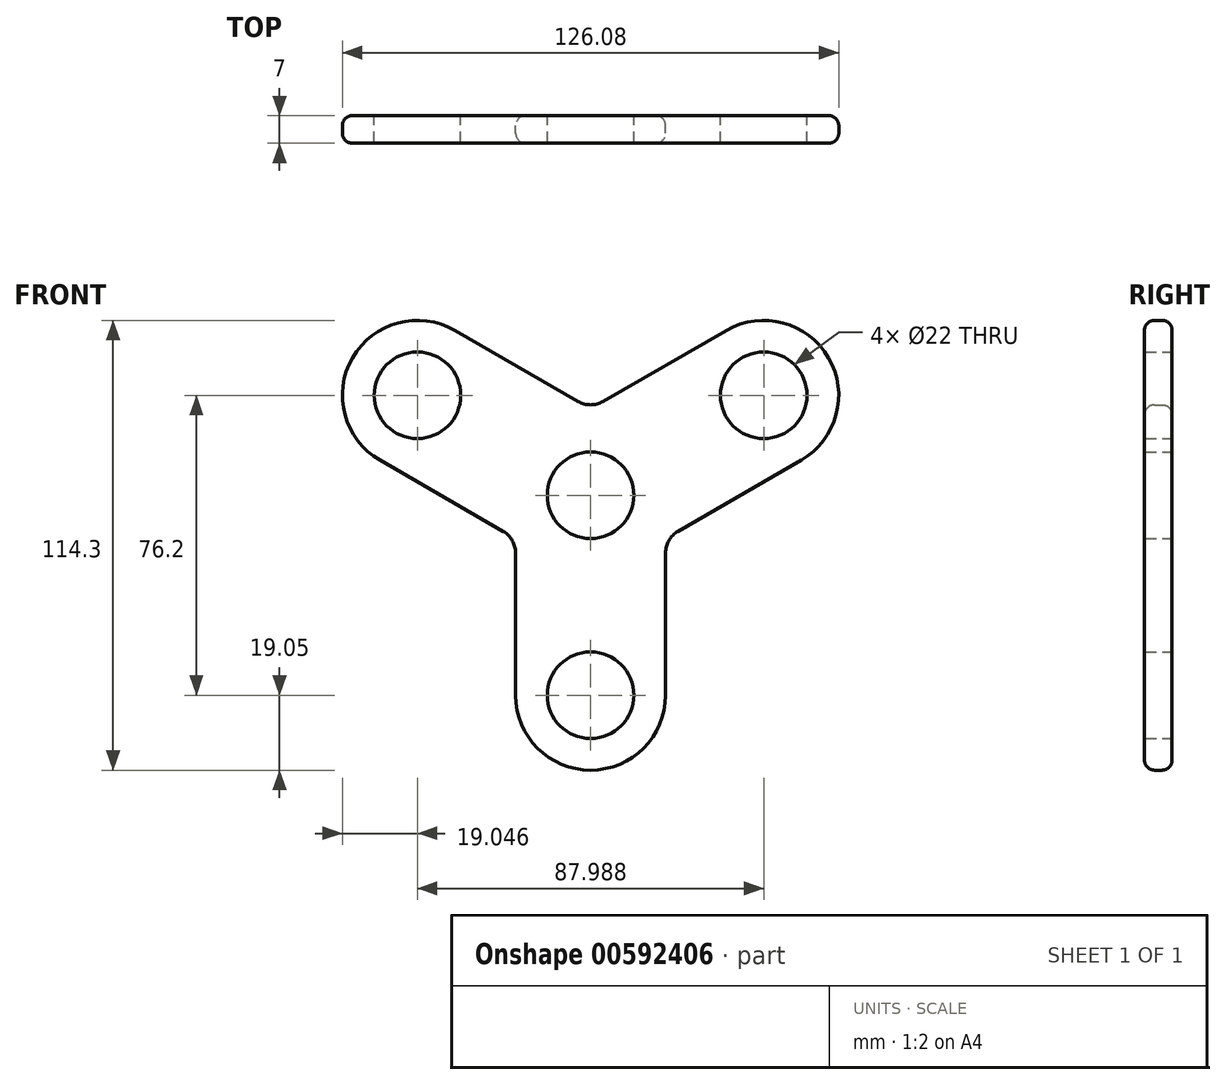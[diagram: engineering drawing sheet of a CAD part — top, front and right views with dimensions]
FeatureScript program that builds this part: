
annotation { "Feature Type Name" : "Feature", "Feature Type Description" : "" }
export const myFeature = defineFeature(function(context is Context, id is Id, definition is map)
    precondition{}
    {
        {
            var Q0;
            Q0=qCreatedBy(makeId("Front.planeOp"),FACE);
            var sketch = newSketch(context, id + "F0", { "sketchPlane" : qUnion([Q0])});
            skCircle(sketch, "E0", {"center": v(0, 6.35) * mm, "radius": 19.05 * mm});
            skCircle(sketch, "E1", {"center": v(-44, 31.75) * mm, "radius": 19.05 * mm});
            skCircle(sketch, "E2", {"center": v(44, 31.75) * mm, "radius": 19.05 * mm});
            skCircle(sketch, "E3", {"center": v(0, -44.45) * mm, "radius": 19.05 * mm});
            skLineSegment(sketch, "E4", {"start": v(-53.52, 15.25) * mm, "end": v(-22.22, -2.82) * mm});
            skLineSegment(sketch, "E5", {"start": v(22.22, -2.82) * mm, "end": v(53.52, 15.25) * mm});
            skLineSegment(sketch, "E6", {"start": v(-19.05, -8.31) * mm, "end": v(-19.05, -44.45) * mm});
            skLineSegment(sketch, "E7", {"start": v(19.05, -8.31) * mm, "end": v(19.05, -44.45) * mm});
            skLineSegment(sketch, "E8", {"start": v(0, 6.35) * mm, "end": v(-44, 31.75) * mm});
            skLineSegment(sketch, "E9", {"start": v(0, 6.35) * mm, "end": v(44, 31.75) * mm});
            skLineSegment(sketch, "E10", {"start": v(0, 6.35) * mm, "end": v(0, -44.45) * mm});
            skCircle(sketch, "E11", {"center": v(0, 6.35) * mm, "radius": 11 * mm});
            skCircle(sketch, "E12", {"center": v(44, 31.75) * mm, "radius": 11 * mm});
            skCircle(sketch, "E13", {"center": v(0, -44.45) * mm, "radius": 11 * mm});
            skCircle(sketch, "E14", {"center": v(-44, 31.75) * mm, "radius": 11 * mm});
            skArc(sketch, "E15.filletArc", {"start": v(-19.05, -8.31) * mm, "mid": v(-19.9, -5.14) * mm, "end": v(-22.22, -2.82) * mm});
            skArc(sketch, "E16.filletArc", {"start": v(22.22, -2.82) * mm, "mid": v(19.9, -5.14) * mm, "end": v(19.05, -8.31) * mm});
            skLineSegment(sketch, "E17", {"start": v(-34.47, 48.25) * mm, "end": v(-3.18, 30.18) * mm});
            skLineSegment(sketch, "E18", {"start": v(34.47, 48.25) * mm, "end": v(3.17, 30.18) * mm});
            skArc(sketch, "E19.filletArc", {"start": v(-3.18, 30.18) * mm, "mid": v(0, 29.33) * mm, "end": v(3.17, 30.18) * mm});
            skSolve(sketch);
        }
        {
            var Q0;
            Q0 = qSketchRegion(id + "F0", true);
            var Q1;
            {var subQ0=sQuery(id+"F0.wireOp",EDGE,"E8");var subQ1=sQuery(id+"F0.wireOp",EDGE,"E0");var subQ2=makeQuery(id+"F0.imprint","INTERSECT",VERTEX,{"derivedFrom":[subQ1,subQ0]});Q1=makeQuery(id+"F0.imprint","IMPRINT",FACE,{"disambiguationData":[TD([[makeQuery(id+"F0.imprint","IMPRINT",EDGE,{"disambiguationData":[TD([[subQ2,-1.0]])],"derivedFrom":subQ1}),1.0]])]});}
            var Q2;
            {var subQ0=sQuery(id+"F0.wireOp",EDGE,"E9");var subQ1=sQuery(id+"F0.wireOp",EDGE,"E0");var subQ2=makeQuery(id+"F0.imprint","INTERSECT",VERTEX,{"derivedFrom":[subQ1,subQ0]});Q2=makeQuery(id+"F0.imprint","IMPRINT",FACE,{"disambiguationData":[TD([[makeQuery(id+"F0.imprint","IMPRINT",EDGE,{"disambiguationData":[TD([[subQ2,1.0]])],"derivedFrom":subQ1}),1.0]])]});}
            var Q3;
            {var subQ0=sQuery(id+"F0.wireOp",EDGE,"E8");var subQ1=sQuery(id+"F0.wireOp",EDGE,"E0");var subQ2=makeQuery(id+"F0.imprint","INTERSECT",VERTEX,{"derivedFrom":[subQ1,subQ0]});Q3=makeQuery(id+"F0.imprint","IMPRINT",FACE,{"disambiguationData":[TD([[makeQuery(id+"F0.imprint","IMPRINT",EDGE,{"disambiguationData":[TD([[subQ2,1.0]])],"derivedFrom":subQ1}),1.0]])]});}
            extrude(context, id + "F1", {"entities" : qUnion([Q0, Q1, Q2, Q3]), "depth" : 7 * mm, "offsetDistance" : 25.4 * mm});
        }
        {
            var Q0;
            Q0=makeQuery(id+"F1.opExtrude","CAP_EDGE",EDGE,{"disambiguationData":[OSD([sQuery(id+"F0.wireOp",EDGE,"E3")])],"isStart":false});
            var Q1;
            Q1=makeQuery(id+"F1.opExtrude","CAP_EDGE",EDGE,{"disambiguationData":[OSD([sQuery(id+"F0.wireOp",EDGE,"E3")])],"isStart":true});
            fillet(context, id + "F2", {"entities" : qUnion([Q0, Q1]), "radius" : 2.54 * mm, "tangentPropagation" : true, "allowEdgeOverflow" : false});
        }
    });
